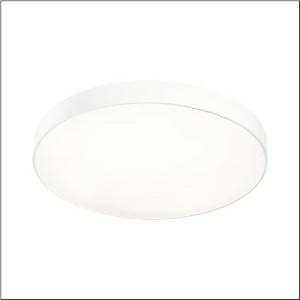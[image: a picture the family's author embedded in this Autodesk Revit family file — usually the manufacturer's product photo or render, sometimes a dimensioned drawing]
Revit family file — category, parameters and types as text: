
# Revit family: round_21_l_51mr38fd0421w
name_source: partatom
category: Lighting Fixtures
units: mm (PartAtom-declared; Revit-internal decimal feet)

## family parameters
Cut with Voids When Loaded = No
Host = Face
Light Source = No
Part Type = Normal
Room Calculation Point = No
Round Connector Dimension = Use Diameter
Shared = No

## types (1)
- Round 21 L (1 x LED, 14150 lm, 97 W, 4000K)
    Apparent Load = 97 VA
    CIE Flux Codes = 49 80 96 100 100
    Color Rendering = 80
    Color Temperature = 4000K
    Default Elevation = 1800 mm
    Description = Round 21 L, wall and ceiling luminaire, primary optical cover: cover, of PMMA, opal, light emission: direct distribution, primary light characteristic: symmetric, installation type: suspended mounting, surface-mounted, LED, rated luminous flux: 13.080lm, luminous efficacy: 146lm/W, light colour: 840, colour temperature: 4000K, control gear: DALI 2, with terminal, 5-pole, mains connection: 230V, AC, 50/60Hz, rated input power: 97W, housing, of aluminium, coated, white, diameter: 850mm, height: 62mm, protection rating (complete): IP40, insulation class (complete): insulation class I (protective earthing), certification: CE, impact resistance: IK04, permissible operating ambient temperature: -10..+35°C, packaging unit: 1 piece
    Height = 87 mm
    Lamp = 1 x LED
    Lamp Light Flux = 14150 lm
    Lamp Power = 97 W
    Lamp count = 1
    Length = 850 mm
    Luminous efficacy = 146 lm/W
    Manufacturer = Siteco
    ModVariant = No
    Model = 51MR38FD0421W
    Mounting Place = Ceiling
    Mounting Type = Surface mounted
    Number of Poles = 1
    OnlyDefault = Yes
    Power Factor = 1
    Product Name = Round 21 L
    Product group = wall and ceiling luminaire
    ProductGroupID = 304
    Protection Class = Protection class I
    Protection Degree = IP 40
    RLX_Detail_Level = 1
    RLX_Emergency_Light_Flux = 0 lm
    RLX_Emergency_Type = 0
    RLX_Emergency_Type_DB = No
    RlxData = <blob elided: 15017 chars, md5=df6223aa>
    Socket = socket
    Standby Power = 0 W
    System Light Flux = 14150 lm
    System Power = 97 W
    Type Comments = Product without accessories
    Type Image = l_1258320.jpg
    URL = http://relux.com
    VarID = ---
    Voltage = 0 V
    Weight = 0.00 kg
    Width = 0 mm  [stored 0 ft]

note: [stored X ft] marks values corroborated as IEEE doubles in the binary element streams (Revit-internal decimal feet)

## geometry (parser evidence)
native form markers: Sweep x12
no freeform markers — native parametric forms only
